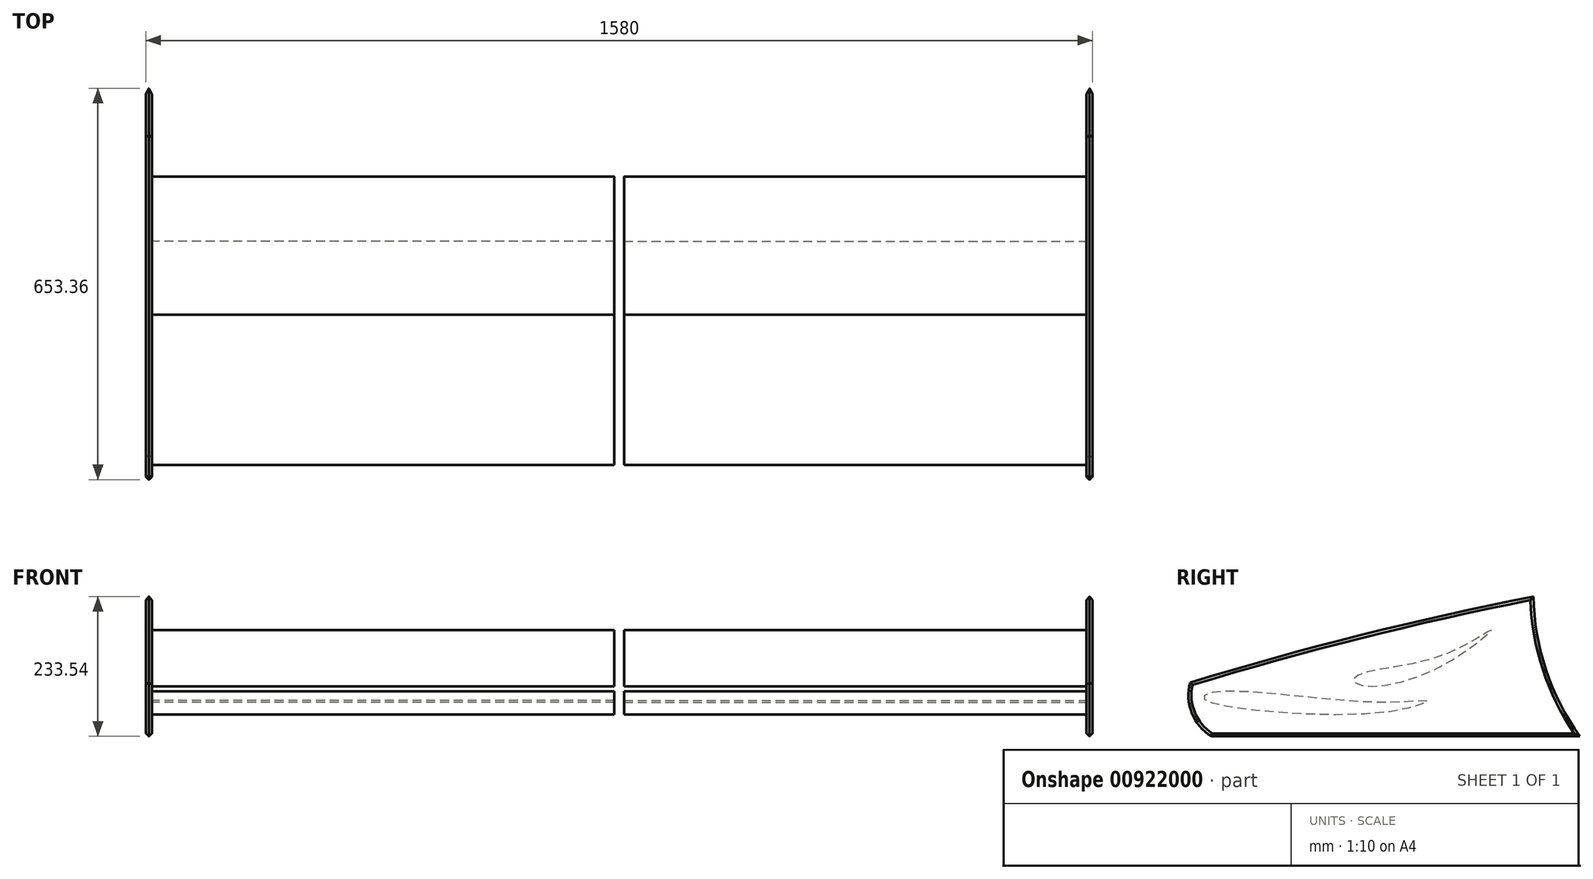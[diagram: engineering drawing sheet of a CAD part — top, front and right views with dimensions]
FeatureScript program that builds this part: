
annotation { "Feature Type Name" : "Feature", "Feature Type Description" : "" }
export const myFeature = defineFeature(function(context is Context, id is Id, definition is map)
    precondition{}
    {
        {
            var Q0;
            Q0=qCreatedBy(makeId("Right.planeOp"),FACE);
            cPlane(context, id + "F0", {"entities" : qUnion([Q0]), "cplaneType" : CPlaneType.OFFSET, "offset" : 780 * mm, "width" : 150 * mm, "height" : 150 * mm});
        }
        {
            var Q0;
            Q0=qCreatedBy(id+"F0.planeOp",FACE);
            var sketch = newSketch(context, id + "F1", { "sketchPlane" : qUnion([Q0])});
            skFitSpline(sketch, "E0", {"points": [v(-1744.88, 58.94) * mm, v(-1817.98, 56.5) * mm, v(-2089.5, 74.94) * mm, v(-2118.25, 65.2) * mm, v(-2091.17, 53.15) * mm, v(-1816.3, 40.58) * mm, v(-1744.88, 58.94) * mm]});
            skFitSpline(sketch, "E1", {"points": [v(-1637.55, 177.22) * mm, v(-1715.24, 136.61) * mm, v(-1851.04, 105.64) * mm, v(-1867.78, 93.67) * mm, v(-1845.73, 83.67) * mm, v(-1709.63, 123.41) * mm, v(-1637.55, 177.22) * mm]});
            skSolve(sketch);
        }
        {
            var Q0;
            Q0=makeQuery(id+"F1.imprint","IMPRINT",FACE,{"disambiguationData":[TD([[makeQuery(id+"F1.imprint","IMPRINT",EDGE,{"derivedFrom":sQuery(id+"F1.wireOp",EDGE,"E0")}),1.0]])]});
            var Q1;
            Q1=makeQuery(id+"F1.imprint","IMPRINT",FACE,{"disambiguationData":[TD([[makeQuery(id+"F1.imprint","IMPRINT",EDGE,{"derivedFrom":sQuery(id+"F1.wireOp",EDGE,"E1")}),1.0]])]});
            extrude(context, id + "F2", {"entities" : qUnion([Q0, Q1]), "oppositeDirection" : true, "depth" : 772 * mm, "offsetDistance" : 25 * mm});
        }
        {
            var Q0;
            Q0=makeQuery(id+"F2.opExtrude","CAP_FACE",FACE,{"disambiguationData":[OSD([sQuery(id+"F1.wireOp",EDGE,"E0")])],"isStart":true});
            var sketch = newSketch(context, id + "F3", { "sketchPlane" : qUnion([Q0])});
            skLineSegment(sketch, "E2", {"start": v(-2104.68, 0) * mm, "end": v(-1489.68, 0) * mm});
            skArc(sketch, "E3", {"start": v(-1489.68, 0) * mm, "mid": v(-1546.14, 110.91) * mm, "end": v(-1567.37, 233.54) * mm});
            skArc(sketch, "E4", {"start": v(-2104.68, 0) * mm, "mid": v(-2137.4, 39.07) * mm, "end": v(-2140.19, 89.96) * mm});
            skArc(sketch, "E5", {"start": v(-2140.19, 89.96) * mm, "mid": v(-1855.56, 168.88) * mm, "end": v(-1567.37, 233.54) * mm});
            skSolve(sketch);
        }
        {
            var Q0;
            Q0=makeQuery(id+"F3.imprint","IMPRINT",FACE,{"disambiguationData":[TD([[makeQuery(id+"F3.imprint","IMPRINT",EDGE,{"derivedFrom":sQuery(id+"F3.wireOp",EDGE,"E2")}),1.0]])]});
            var Q1;
            Q1=makeQuery(id+"F3.imprint","IMPRINT",FACE,{"disambiguationData":[TD([[makeQuery(id+"F3.imprint","IMPRINT",EDGE,{"derivedFrom":makeQuery(id+"F2.opExtrude","CAP_EDGE",EDGE,{"disambiguationData":[OSD([sQuery(id+"F1.wireOp",EDGE,"E0")])],"isStart":true})}),1.0]])]});
            extrude(context, id + "F4", {"entities" : qUnion([Q0, Q1]), "depth" : 10 * mm, "offsetDistance" : 25 * mm});
        }
        {
            var Q0;
            Q0=makeQuery(id+"F4.opExtrude","CAP_FACE",FACE,{"disambiguationData":[OSD([sQuery(id+"F3.wireOp",EDGE,"E2"),sQuery(id+"F3.wireOp",EDGE,"E3"),sQuery(id+"F3.wireOp",EDGE,"E4"),sQuery(id+"F3.wireOp",EDGE,"E5")])],"isStart":true});
            var Q1;
            Q1=makeQuery(id+"F4.opExtrude","CAP_FACE",FACE,{"disambiguationData":[OSD([sQuery(id+"F3.wireOp",EDGE,"E2"),sQuery(id+"F3.wireOp",EDGE,"E3"),sQuery(id+"F3.wireOp",EDGE,"E4"),sQuery(id+"F3.wireOp",EDGE,"E5")])],"isStart":false});
            chamfer(context, id + "F5", {"entities" : qUnion([Q0, Q1]), "width" : 5 * mm, "tangentPropagation" : true});
        }
        {
            var Q0;
            Q0=makeQuery(id+"F2.opExtrude","SWEPT_BODY",BODY,{"disambiguationData":[OSD([sQuery(id+"F1.wireOp",EDGE,"E1")])]});
            var Q1;
            Q1=makeQuery(id+"F2.opExtrude","SWEPT_BODY",BODY,{"disambiguationData":[OSD([sQuery(id+"F1.wireOp",EDGE,"E0")])]});
            var Q2;
            Q2=makeQuery(id+"F4.opExtrude","SWEPT_BODY",BODY,{"disambiguationData":[OSD([sQuery(id+"F3.wireOp",EDGE,"E2"),sQuery(id+"F3.wireOp",EDGE,"E3"),sQuery(id+"F3.wireOp",EDGE,"E4"),sQuery(id+"F3.wireOp",EDGE,"E5")])]});
            var Q3;
            Q3=qCreatedBy(makeId("Right.planeOp"),FACE);
            mirror(context, id + "F6", {"entities" : qUnion([Q0, Q1, Q2]), "mirrorPlane" : qUnion([Q3])});
        }
    });
